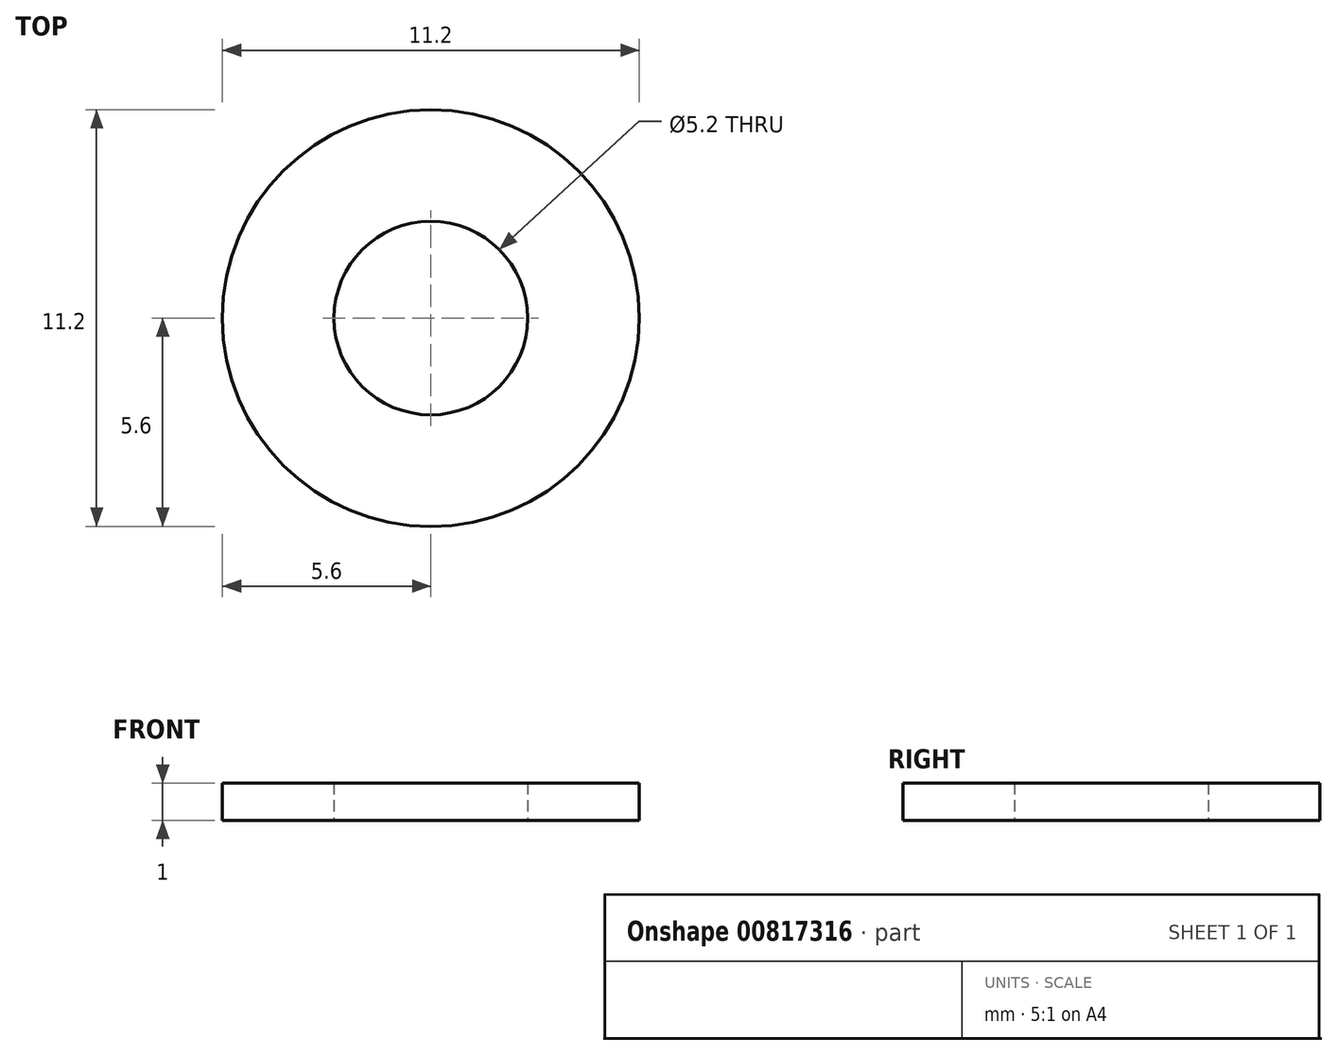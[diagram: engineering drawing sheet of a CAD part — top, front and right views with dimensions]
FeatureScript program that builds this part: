
annotation { "Feature Type Name" : "Feature", "Feature Type Description" : "" }
export const myFeature = defineFeature(function(context is Context, id is Id, definition is map)
    precondition{}
    {
        {
            var Q0;
            Q0=qCreatedBy(makeId("Top.planeOp"),FACE);
            var sketch = newSketch(context, id + "F0", { "sketchPlane" : qUnion([Q0])});
            skCircle(sketch, "E0", {"center": v(0, 0) * mm, "radius": 5.6 * mm});
            skCircle(sketch, "E1", {"center": v(0, 0) * mm, "radius": 2.6 * mm});
            skSolve(sketch);
        }
        {
            var Q0;
            Q0=makeQuery(id+"F0.imprint","IMPRINT",FACE,{"disambiguationData":[TD([[makeQuery(id+"F0.imprint","IMPRINT",EDGE,{"derivedFrom":sQuery(id+"F0.wireOp",EDGE,"E0")}),1.0]])]});
            extrude(context, id + "F1", {"entities" : qUnion([Q0]), "depth" : 1 * mm, "offsetDistance" : 25 * mm});
        }
    });
